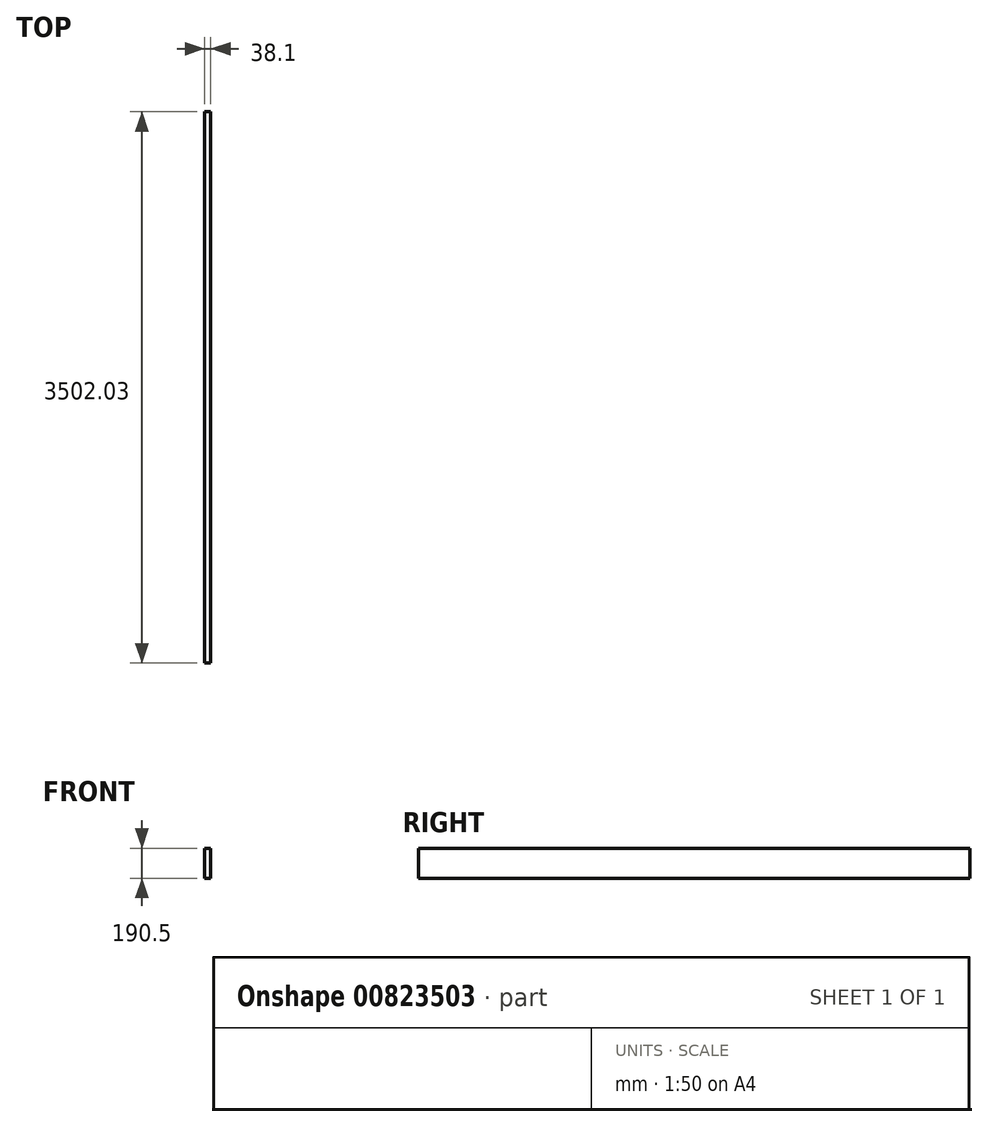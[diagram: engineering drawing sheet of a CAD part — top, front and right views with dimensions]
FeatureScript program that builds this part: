
annotation { "Feature Type Name" : "Feature", "Feature Type Description" : "" }
export const myFeature = defineFeature(function(context is Context, id is Id, definition is map)
    precondition{}
    {
        {
            var Q0;
            Q0=qCreatedBy(makeId("Front.planeOp"),FACE);
            var sketch = newSketch(context, id + "F0", { "sketchPlane" : qUnion([Q0])});
            skLineSegment(sketch, "E0.bottom", {"start": v(0, 0) * mm, "end": v(38.1, 0) * mm});
            skLineSegment(sketch, "E0.top", {"start": v(0, 190.5) * mm, "end": v(38.1, 190.5) * mm});
            skLineSegment(sketch, "E0.left", {"start": v(0, 0) * mm, "end": v(0, 190.5) * mm});
            skLineSegment(sketch, "E0.right", {"start": v(38.1, 0) * mm, "end": v(38.1, 190.5) * mm});
            skSolve(sketch);
        }
        {
            var Q0;
            Q0=qSketchRegion(id+"F0",true);
            extrude(context, id + "F1", {"entities" : qUnion([Q0]), "depth" : 3502.02 * mm, "offsetDistance" : 25.4 * mm});
        }
    });
